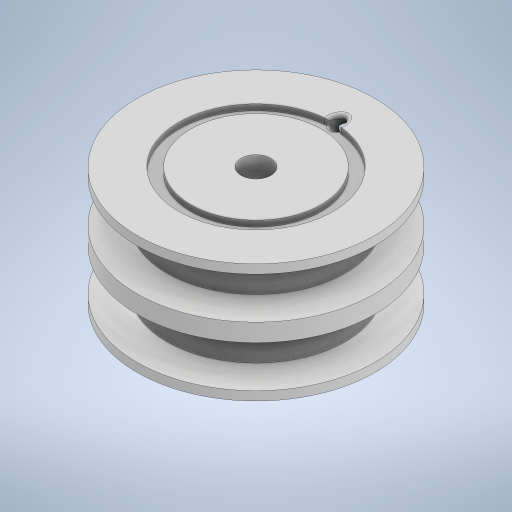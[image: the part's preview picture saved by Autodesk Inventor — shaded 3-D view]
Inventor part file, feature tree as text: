
AUTODESK INVENTOR PART (.ipt)
format: ipt  version: 2023.1 (Build 271208000, 208)  size: 450,560 bytes
history: native  units: mm
features: sketch x8, extrude x5, other x2, revolve x2, mirror x2, fillet x2
ambient origin geometry x8: Origin, YZ Plane, XZ Plane, XY Plane, X Axis, Y Axis, Z Axis, Center Point
bodies: Body1 (feature_tree)
feature tree (21):
  other  "솔리드1"
  extrude  "돌출1"  Depth=9.0mm
  extrude  "돌출2"  Depth=5.8mm
  extrude  "돌출3"  Depth=0.5mm
  sketch  "스케치4"
  revolve  "회전1"
  revolve  "회전2"
  mirror  "미러1"
  extrude  "돌출4"  Depth=6.0mm TaperAngle=0.0deg
  fillet  "모깎기1"  Radius=1.0mm
  extrude  "돌출5"  Depth=3.0mm
  other  "작업 평면1"
  mirror  "미러2"
  fillet  "모깎기3"  Radius=2.0mm
  sketch  "스케치1"
  sketch  "스케치2"
  sketch  "스케치3"
  sketch  "스케치5"
  sketch  "스케치6"
  sketch  "스케치7"
  sketch  "스케치8"
